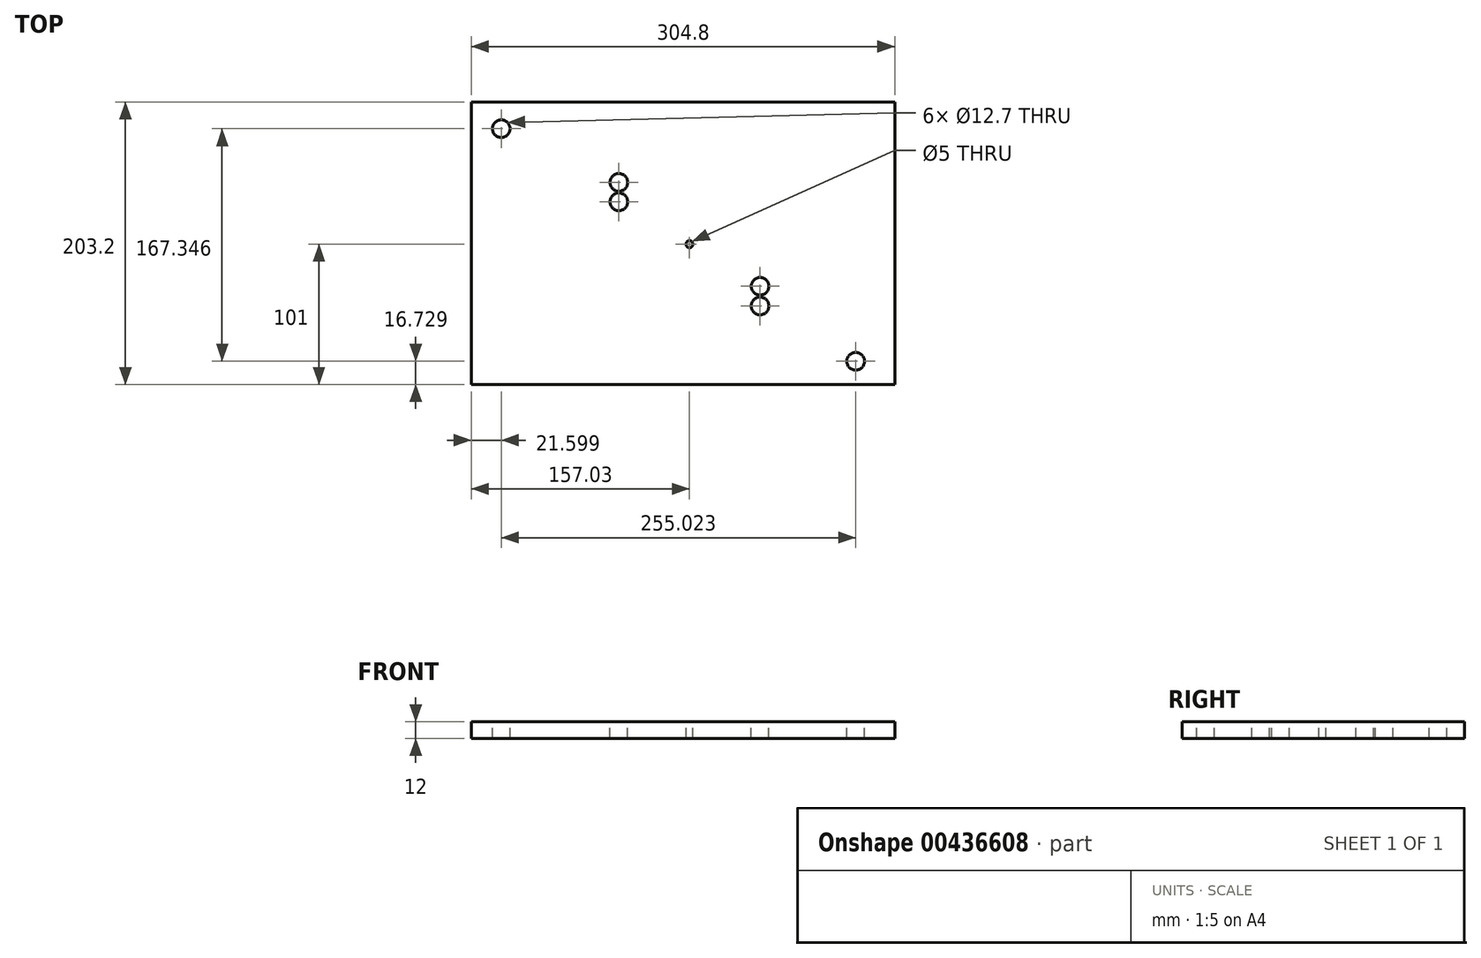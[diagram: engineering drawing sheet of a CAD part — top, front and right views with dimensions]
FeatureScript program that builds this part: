
annotation { "Feature Type Name" : "Feature", "Feature Type Description" : "" }
export const myFeature = defineFeature(function(context is Context, id is Id, definition is map)
    precondition{}
    {
        {
            var Q0;
            Q0=qCreatedBy(makeId("Top.planeOp"),FACE);
            var sketch = newSketch(context, id + "F0", { "sketchPlane" : qUnion([Q0])});
            skLineSegment(sketch, "E0.bottom", {"start": v(-157.03, 102.2) * mm, "end": v(147.77, 102.2) * mm});
            skLineSegment(sketch, "E0.top", {"start": v(-157.03, -101) * mm, "end": v(147.77, -101) * mm});
            skLineSegment(sketch, "E0.left", {"start": v(-157.03, 102.2) * mm, "end": v(-157.03, -101) * mm});
            skLineSegment(sketch, "E0.right", {"start": v(147.77, 102.2) * mm, "end": v(147.77, -101) * mm});
            skCircle(sketch, "E1", {"center": v(50.8, -30.26) * mm, "radius": 6.35 * mm});
            skCircle(sketch, "E2", {"center": v(50.8, -44.45) * mm, "radius": 6.35 * mm});
            skCircle(sketch, "E3", {"center": v(-50.8, 44.45) * mm, "radius": 6.35 * mm});
            skCircle(sketch, "E4", {"center": v(-50.8, 30.48) * mm, "radius": 6.35 * mm});
            skCircle(sketch, "E5", {"center": v(119.6, -84.27) * mm, "radius": 6.35 * mm});
            skCircle(sketch, "E6", {"center": v(-135.43, 83.08) * mm, "radius": 6.35 * mm});
            skCircle(sketch, "E7", {"center": v(119.6, -84.27) * mm, "radius": 2 * mm});
            skCircle(sketch, "E8", {"center": v(50.8, -44.45) * mm, "radius": 2 * mm});
            skCircle(sketch, "E9", {"center": v(50.8, -30.26) * mm, "radius": 2 * mm});
            skCircle(sketch, "E10", {"center": v(-50.8, 44.45) * mm, "radius": 2 * mm});
            skCircle(sketch, "E11", {"center": v(-50.8, 30.48) * mm, "radius": 2 * mm});
            skCircle(sketch, "E12", {"center": v(-135.43, 83.08) * mm, "radius": 2 * mm});
            skSolve(sketch);
        }
        {
            var Q0;
            Q0=makeQuery(id+"F0.imprint","IMPRINT",FACE,{"disambiguationData":[TD([[makeQuery(id+"F0.imprint","IMPRINT",EDGE,{"derivedFrom":sQuery(id+"F0.wireOp",EDGE,"E0.bottom")}),-1.0]])]});
            extrude(context, id + "F1", {"entities" : qUnion([Q0]), "depth" : -12 * mm});
        }
        {
            var Q0;
            Q0=makeQuery(id+"F1.opExtrude","CAP_FACE",FACE,{"disambiguationData":[OSD([sQuery(id+"F0.wireOp",EDGE,"E0.bottom"),sQuery(id+"F0.wireOp",EDGE,"E0.top"),sQuery(id+"F0.wireOp",EDGE,"E0.left"),sQuery(id+"F0.wireOp",EDGE,"E0.right"),sQuery(id+"F0.wireOp",EDGE,"E1"),sQuery(id+"F0.wireOp",EDGE,"E2"),sQuery(id+"F0.wireOp",EDGE,"E3"),sQuery(id+"F0.wireOp",EDGE,"E4"),sQuery(id+"F0.wireOp",EDGE,"E5"),sQuery(id+"F0.wireOp",EDGE,"E6")])],"isStart":true});
            var sketch = newSketch(context, id + "F2", { "sketchPlane" : qUnion([Q0])});
            skCircle(sketch, "E13", {"center": v(0, 0) * mm, "radius": 5.06 * mm});
            skSolve(sketch);
        }
        {
            var Q0;
            Q0=sQuery(id+"F2.wireOp",VERTEX,"E13.center");
            var Q1;
            Q1=makeQuery(id+"F1.opExtrude","SWEPT_BODY",BODY,{"disambiguationData":[OSD([sQuery(id+"F0.wireOp",EDGE,"E0.bottom"),sQuery(id+"F0.wireOp",EDGE,"E0.top"),sQuery(id+"F0.wireOp",EDGE,"E0.left"),sQuery(id+"F0.wireOp",EDGE,"E0.right"),sQuery(id+"F0.wireOp",EDGE,"E1"),sQuery(id+"F0.wireOp",EDGE,"E2"),sQuery(id+"F0.wireOp",EDGE,"E3"),sQuery(id+"F0.wireOp",EDGE,"E4"),sQuery(id+"F0.wireOp",EDGE,"E5"),sQuery(id+"F0.wireOp",EDGE,"E6")])]});
            hole(context, id + "F3", {"style" : HoleStyle.SIMPLE, "endStyle" : HoleEndStyle.THROUGH, "holeDiameter" : 5 * mm, "isTappedThrough" : true, "tappedDepth" : 7.75 * mm, "tapClearance" : 3, "startFromSketch" : true, "locations" : qUnion([Q0]), "scope" : qUnion([Q1])});
        }
    });
